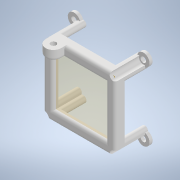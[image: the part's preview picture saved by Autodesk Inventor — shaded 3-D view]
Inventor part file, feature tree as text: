
AUTODESK INVENTOR PART (.ipt)
format: ipt  version: 2021 (Build 250183000, 183)  size: 312,832 bytes
history: native  units: mm
features: sketch x7, extrude x6, projected_geometry x5, fillet x4, other x3, reference x2, plane x1, hole x1
ambient origin geometry x8: Origin, YZ Plane, XZ Plane, XY Plane, X Axis, Y Axis, Z Axis, Center Point
bodies: Solid1 (feature_tree)
feature tree (29):
  plane  "Work Plane1"
  extrude  "Extrusion1"  Depth=4.0mm
  extrude  "Extrusion2"  Depth=2.0mm
  extrude  "Extrusion3"  Depth=2.0mm
  extrude  "Extrusion4"  Depth=1.0mm
  extrude  "Extrusion5"  Depth=19.0mm TaperAngle=0.0deg
  fillet  "Fillet1"  Radius=3.5mm
  extrude  "Extrusion6"  Depth=2.0mm TaperAngle=0.0deg
  fillet  "Fillet2"  Radius=2.0mm
  hole  "Hole1"  [1 undecoded]
  fillet  "Fillet3"  Radius=7.0mm
  fillet  "Fillet4"  Radius=5.0mm
  sketch  "Sketch1"  dims[d0=0.4mm d1=4.0mm]
  reference  "Reference1"
  sketch  "Sketch2"  dims[d2=4.0mm d3=0.0mm d4=2.0mm]
  reference  "Reference2"
  sketch  "Sketch3"  dims[d5=2.0mm d6=0.0mm d7=5.5mm]
  sketch  "Sketch4"  dims[d8=1.0mm d9=1.0mm]
  projected_geometry  "Projected Loop1"
  projected_geometry  "Projected Loop2"
  projected_geometry  "Projected Loop3"
  projected_geometry  "Projected Loop4"
  projected_geometry  "Projected Loop5"
  sketch  "Sketch5"  dims[d10=15.0mm d11=0.0mm d12=19.0mm d13=0.0mm d14=3.5mm]
  sketch  "Sketch6"  dims[d15=8.0mm d16=2.0mm d17=0.0mm d18=2.0mm]
  sketch  "Sketch7"  dims[d19=10.0mm d20=6.4mm d21=7.0mm d22=0.0mm d23=5.0mm d24=3.5mm d25=6.0mm d26=5.6mm d27=2.4mm d28=90.0deg d29=8.0mm d30=20.594885mm d31=2.0mm d32=2.0mm]
  parser-record x1  (decoder bookkeeping rows leaked as tree rows — omitted from the tree; the rows remain in map.json)
  other  "Heatsink Holder.iam"
  other  "Heatsink:1"
note: 1 required parameter value undecoded (feature->parameter linkage not recoverable at this tier; creation-order binding heuristic only, values carry confidence <= 0.55)
note: 1 file-system path scrubbed to <path> (originals preserved in map.json)
